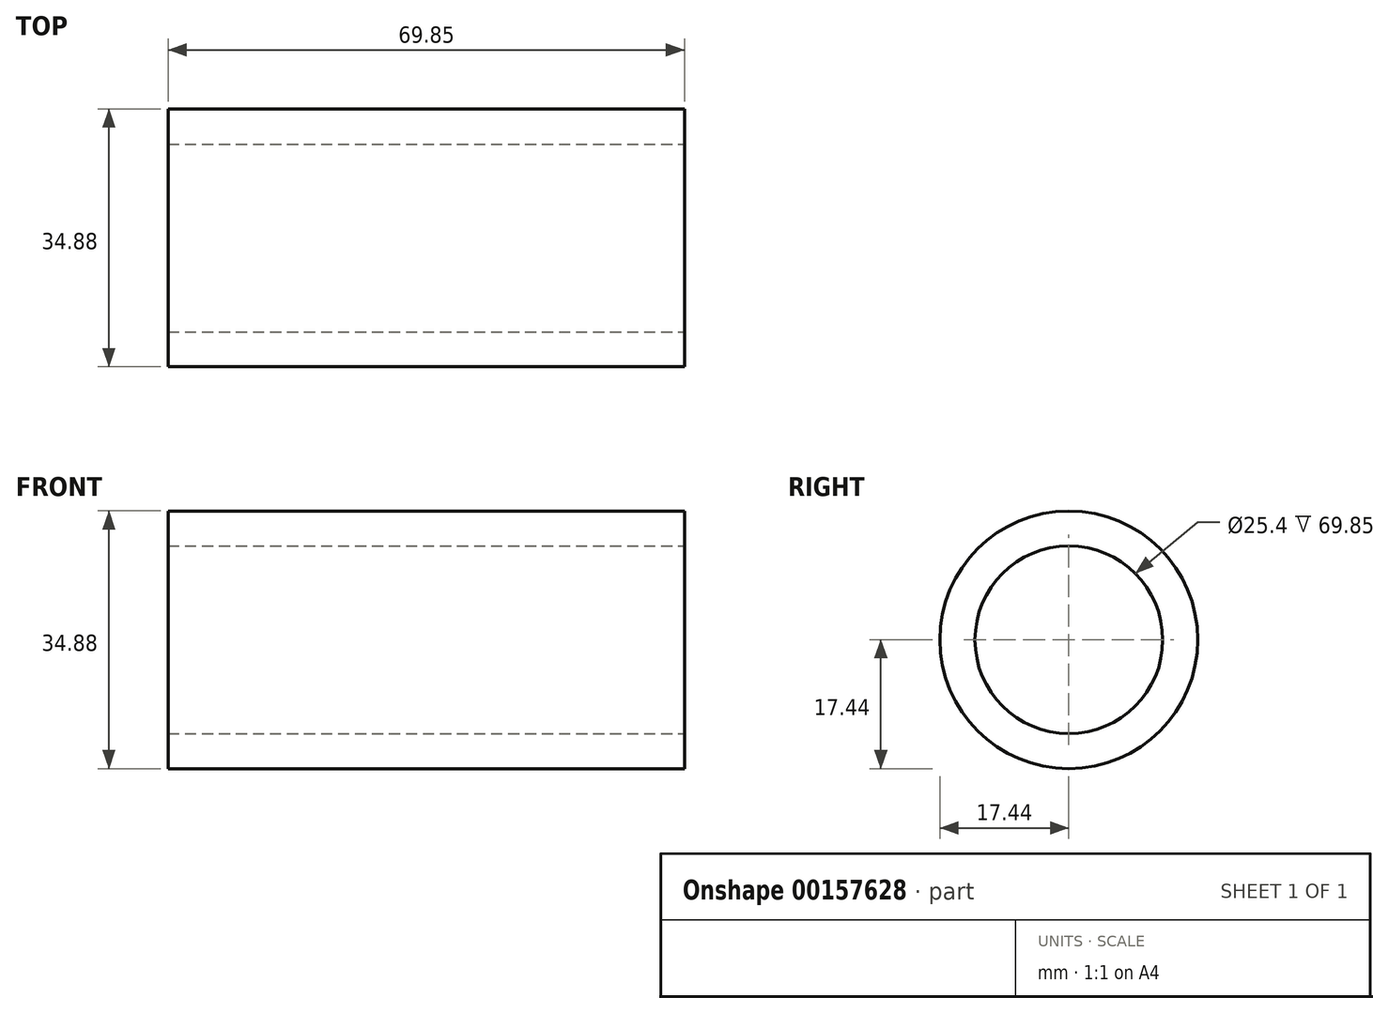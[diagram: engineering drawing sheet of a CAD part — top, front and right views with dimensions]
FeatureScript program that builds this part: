
annotation { "Feature Type Name" : "Feature", "Feature Type Description" : "" }
export const myFeature = defineFeature(function(context is Context, id is Id, definition is map)
    precondition{}
    {
        {
            var Q0;
            Q0=qCreatedBy(makeId("Right.planeOp"),FACE);
            var sketch = newSketch(context, id + "F0", { "sketchPlane" : qUnion([Q0])});
            skCircle(sketch, "E0", {"center": v(0, 0) * mm, "radius": 12.7 * mm});
            skCircle(sketch, "E1", {"center": v(0, 0) * mm, "radius": 17.44 * mm});
            skSolve(sketch);
        }
        {
            var Q0;
            Q0=makeQuery(id+"F0.imprint","IMPRINT",FACE,{"disambiguationData":[TD([[makeQuery(id+"F0.imprint","IMPRINT",EDGE,{"derivedFrom":sQuery(id+"F0.wireOp",EDGE,"E0")}),-1.0]])]});
            extrude(context, id + "F1", {"entities" : qUnion([Q0]), "oppositeDirection" : true, "depth" : 69.85 * mm});
        }
    });
